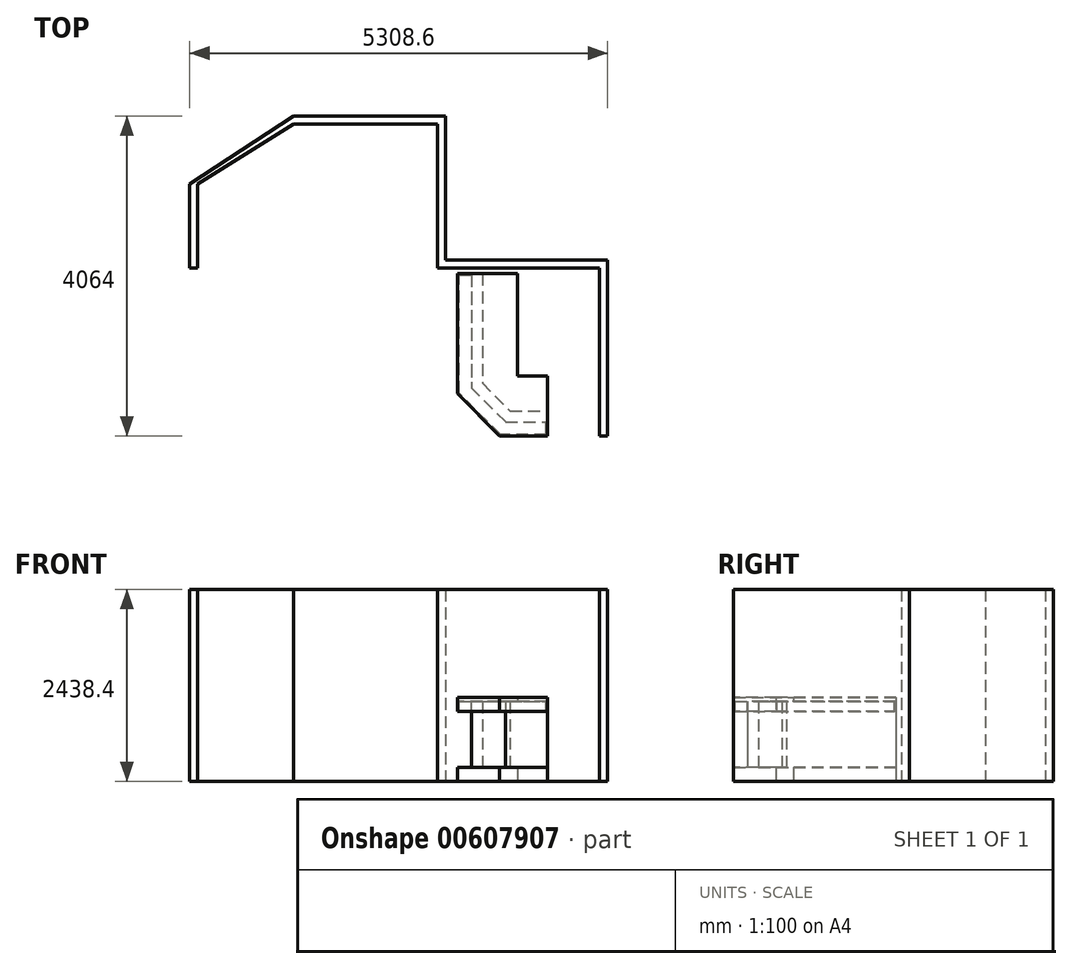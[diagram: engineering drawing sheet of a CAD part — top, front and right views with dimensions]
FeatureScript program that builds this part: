
annotation { "Feature Type Name" : "Feature", "Feature Type Description" : "" }
export const myFeature = defineFeature(function(context is Context, id is Id, definition is map)
    precondition{}
    {
        {
            var Q0;
            Q0=qCreatedBy(makeId("Top.planeOp"),FACE);
            var sketch = newSketch(context, id + "F0", { "sketchPlane" : qUnion([Q0])});
            skLineSegment(sketch, "E0", {"start": v(0, 0) * mm, "end": v(0, 2133.6) * mm});
            skLineSegment(sketch, "E1", {"start": v(0, 2133.6) * mm, "end": v(-2057.4, 2133.6) * mm});
            skLineSegment(sketch, "E2", {"start": v(-2057.4, 2133.6) * mm, "end": v(-2057.4, 3962.4) * mm});
            skLineSegment(sketch, "E3", {"start": v(-2057.4, 3962.4) * mm, "end": v(-3886.2, 3962.4) * mm});
            skLineSegment(sketch, "E4", {"start": v(-3886.2, 3962.4) * mm, "end": v(-5105.4, 3200.4) * mm});
            skLineSegment(sketch, "E5", {"start": v(-5105.4, 3200.4) * mm, "end": v(-5105.4, 2133.6) * mm});
            skLineSegment(sketch, "E6", {"start": v(-5105.4, 2133.6) * mm, "end": v(-5207, 2133.6) * mm});
            skLineSegment(sketch, "E7", {"start": v(-5207, 2133.6) * mm, "end": v(-5207, 3200.4) * mm});
            skLineSegment(sketch, "E8", {"start": v(-5207, 3200.4) * mm, "end": v(-3886.2, 4064) * mm});
            skLineSegment(sketch, "E9", {"start": v(-3886.2, 4064) * mm, "end": v(-1955.8, 4064) * mm});
            skLineSegment(sketch, "E10", {"start": v(-1955.8, 2235.2) * mm, "end": v(101.6, 2235.2) * mm});
            skLineSegment(sketch, "E11", {"start": v(101.6, 2235.2) * mm, "end": v(101.6, 0) * mm});
            skLineSegment(sketch, "E12", {"start": v(-1955.8, 4064) * mm, "end": v(-1955.8, 2235.2) * mm});
            skLineSegment(sketch, "E13", {"start": v(101.6, 0) * mm, "end": v(0, 0) * mm});
            skSolve(sketch);
        }
        {
            var Q0;
            Q0=makeQuery(id+"F0.imprint","IMPRINT",FACE,{"disambiguationData":[TD([[makeQuery(id+"F0.imprint","IMPRINT",EDGE,{"derivedFrom":sQuery(id+"F0.wireOp",EDGE,"E0")}),-1.0]])]});
            extrude(context, id + "F1", {"entities" : qUnion([Q0]), "depth" : 2438.4 * mm, "offsetDistance" : 25.4 * mm});
        }
        {
            var Q0;
            Q0=qCreatedBy(makeId("Top.planeOp"),FACE);
            var sketch = newSketch(context, id + "F2", { "sketchPlane" : qUnion([Q0])});
            skLineSegment(sketch, "E14", {"start": v(-1046.82, 2062.82) * mm, "end": v(-1808.82, 2062.82) * mm});
            skLineSegment(sketch, "E15", {"start": v(-1808.82, 2062.82) * mm, "end": v(-1808.82, 538.82) * mm});
            skLineSegment(sketch, "E16", {"start": v(-1808.82, 538.82) * mm, "end": v(-1270, 0) * mm});
            skLineSegment(sketch, "E17", {"start": v(-1270, 0) * mm, "end": v(-660.4, 0) * mm});
            skLineSegment(sketch, "E18", {"start": v(-660.4, 0) * mm, "end": v(-660.4, 762) * mm});
            skLineSegment(sketch, "E19", {"start": v(-660.4, 762) * mm, "end": v(-1046.82, 762) * mm});
            skLineSegment(sketch, "E20", {"start": v(-1046.82, 762) * mm, "end": v(-1046.82, 2062.82) * mm});
            skSolve(sketch);
        }
        {
            var Q0;
            Q0=makeQuery(id+"F2.imprint","IMPRINT",FACE,{"disambiguationData":[TD([[makeQuery(id+"F2.imprint","IMPRINT",EDGE,{"derivedFrom":sQuery(id+"F2.wireOp",EDGE,"E14")}),1.0]])]});
            extrude(context, id + "F3", {"entities" : qUnion([Q0]), "depth" : 177.8 * mm, "offsetDistance" : 25.4 * mm});
        }
        {
            var Q0;
            Q0=makeQuery(id+"F3.opExtrude","CAP_FACE",FACE,{"disambiguationData":[OSD([sQuery(id+"F2.wireOp",EDGE,"E14"),sQuery(id+"F2.wireOp",EDGE,"E15"),sQuery(id+"F2.wireOp",EDGE,"E16"),sQuery(id+"F2.wireOp",EDGE,"E17"),sQuery(id+"F2.wireOp",EDGE,"E18"),sQuery(id+"F2.wireOp",EDGE,"E19"),sQuery(id+"F2.wireOp",EDGE,"E20")])],"isStart":false});
            var sketch = newSketch(context, id + "F4", { "sketchPlane" : qUnion([Q0])});
            skLineSegment(sketch, "E21", {"start": v(-1631.02, 2062.82) * mm, "end": v(-1631.02, 612.46) * mm});
            skLineSegment(sketch, "E22", {"start": v(-1631.02, 612.46) * mm, "end": v(-1196.35, 177.8) * mm});
            skLineSegment(sketch, "E23", {"start": v(-1196.35, 177.8) * mm, "end": v(-660.4, 177.8) * mm});
            skLineSegment(sketch, "E24", {"start": v(-1491.32, 2062.82) * mm, "end": v(-1631.02, 2062.82) * mm});
            skLineSegment(sketch, "E25", {"start": v(-1491.32, 2062.82) * mm, "end": v(-1491.32, 670.33) * mm});
            skLineSegment(sketch, "E26", {"start": v(-1491.32, 670.33) * mm, "end": v(-1138.49, 317.5) * mm});
            skLineSegment(sketch, "E27", {"start": v(-660.4, 177.8) * mm, "end": v(-660.4, 317.5) * mm});
            skLineSegment(sketch, "E28", {"start": v(-1138.49, 317.5) * mm, "end": v(-660.4, 317.5) * mm});
            skSolve(sketch);
        }
        {
            var Q0;
            Q0=makeQuery(id+"F4.imprint","IMPRINT",FACE,{"disambiguationData":[TD([[makeQuery(id+"F4.imprint","IMPRINT",EDGE,{"derivedFrom":sQuery(id+"F4.wireOp",EDGE,"E21")}),1.0]])]});
            extrude(context, id + "F5", {"entities" : qUnion([Q0]), "operationType" : NewBodyOperationType.ADD, "depth" : 838.2 * mm, "offsetDistance" : 25.4 * mm});
        }
        {
            var Q0;
            Q0=makeQuery(id+"F5.opExtrude","CAP_FACE",FACE,{"disambiguationData":[OSD([sQuery(id+"F4.wireOp",EDGE,"E21"),sQuery(id+"F4.wireOp",EDGE,"E22"),sQuery(id+"F4.wireOp",EDGE,"E23"),sQuery(id+"F4.wireOp",EDGE,"E24"),sQuery(id+"F4.wireOp",EDGE,"E25"),sQuery(id+"F4.wireOp",EDGE,"E26"),sQuery(id+"F4.wireOp",EDGE,"E27"),sQuery(id+"F4.wireOp",EDGE,"E28")])],"isStart":false});
            var sketch = newSketch(context, id + "F6", { "sketchPlane" : qUnion([Q0])});
            skLineSegment(sketch, "E29", {"start": v(-1808.82, 2062.82) * mm, "end": v(-1808.82, 538.82) * mm});
            skLineSegment(sketch, "E30", {"start": v(-1808.82, 538.82) * mm, "end": v(-1270, 0) * mm});
            skLineSegment(sketch, "E31", {"start": v(-1270, 0) * mm, "end": v(-660.4, 0) * mm});
            skLineSegment(sketch, "E32", {"start": v(-660.4, 0) * mm, "end": v(-660.4, 762) * mm});
            skLineSegment(sketch, "E33", {"start": v(-660.4, 762) * mm, "end": v(-1046.82, 762) * mm});
            skLineSegment(sketch, "E34", {"start": v(-1046.82, 762) * mm, "end": v(-1046.82, 2062.82) * mm});
            skLineSegment(sketch, "E35", {"start": v(-1046.82, 2062.82) * mm, "end": v(-1808.82, 2062.82) * mm});
            skSolve(sketch);
        }
        {
            var Q0;
            Q0 = qSketchRegion(id + "F6", true);
            extrude(context, id + "F7", {"entities" : qUnion([Q0]), "operationType" : NewBodyOperationType.ADD, "depth" : 50.8 * mm, "offsetDistance" : 25.4 * mm});
        }
        {
            var Q0;
            {var subQ0=sQuery(id+"F6.wireOp",EDGE,"E31");var subQ1=sQuery(id+"F6.wireOp",EDGE,"E30");var subQ2=sQuery(id+"F6.wireOp",EDGE,"E29");var subQ3=sQuery(id+"F6.wireOp",EDGE,"E32");var subQ4=sQuery(id+"F6.wireOp",EDGE,"E35");Q0=makeQuery(id+"F7.boolean.opBoolean","SPLIT",FACE,{"disambiguationData":[TD([makeQuery(id+"F5.opExtrude","SWEPT_FACE",FACE,{"disambiguationData":[OSD([sQuery(id+"F4.wireOp",EDGE,"E21")])]})])],"derivedFrom":makeQuery(id+"F7.opExtrude","CAP_FACE",FACE,{"disambiguationData":[OSD([subQ2,subQ1,subQ0,subQ3,sQuery(id+"F6.wireOp",EDGE,"E33"),sQuery(id+"F6.wireOp",EDGE,"E34"),subQ4])],"isStart":true})});}
            var sketch = newSketch(context, id + "F8", { "sketchPlane" : qUnion([Q0])});
            skLineSegment(sketch, "E36", {"start": v(-1808.82, -2062.82) * mm, "end": v(-1808.82, -538.82) * mm});
            skLineSegment(sketch, "E37", {"start": v(-1808.82, -538.82) * mm, "end": v(-1270, 0) * mm});
            skLineSegment(sketch, "E38", {"start": v(-1270, 0) * mm, "end": v(-660.4, 0) * mm});
            skLineSegment(sketch, "E39", {"start": v(-679.45, -19.05) * mm, "end": v(-1262.1, -19.05) * mm});
            skLineSegment(sketch, "E40", {"start": v(-1262.1, -19.05) * mm, "end": v(-1789.77, -546.7) * mm});
            skLineSegment(sketch, "E41", {"start": v(-1789.77, -546.7) * mm, "end": v(-1789.77, -2043.77) * mm});
            skLineSegment(sketch, "E42", {"start": v(-679.45, -19.05) * mm, "end": v(-679.45, -177.8) * mm});
            skLineSegment(sketch, "E43", {"start": v(-679.45, -177.8) * mm, "end": v(-660.4, -177.8) * mm});
            skLineSegment(sketch, "E44", {"start": v(-660.4, -177.8) * mm, "end": v(-660.4, 0) * mm});
            skLineSegment(sketch, "E45", {"start": v(-1789.77, -2043.77) * mm, "end": v(-1631.02, -2043.77) * mm});
            skLineSegment(sketch, "E46", {"start": v(-1631.02, -2043.77) * mm, "end": v(-1631.02, -2062.82) * mm});
            skLineSegment(sketch, "E47", {"start": v(-1808.82, -2062.82) * mm, "end": v(-1631.02, -2062.82) * mm});
            skSolve(sketch);
        }
        {
            var Q0;
            Q0 = qSketchRegion(id + "F8", true);
            extrude(context, id + "F9", {"entities" : qUnion([Q0]), "operationType" : NewBodyOperationType.ADD, "depth" : 127 * mm, "offsetDistance" : 25.4 * mm});
        }
    });
